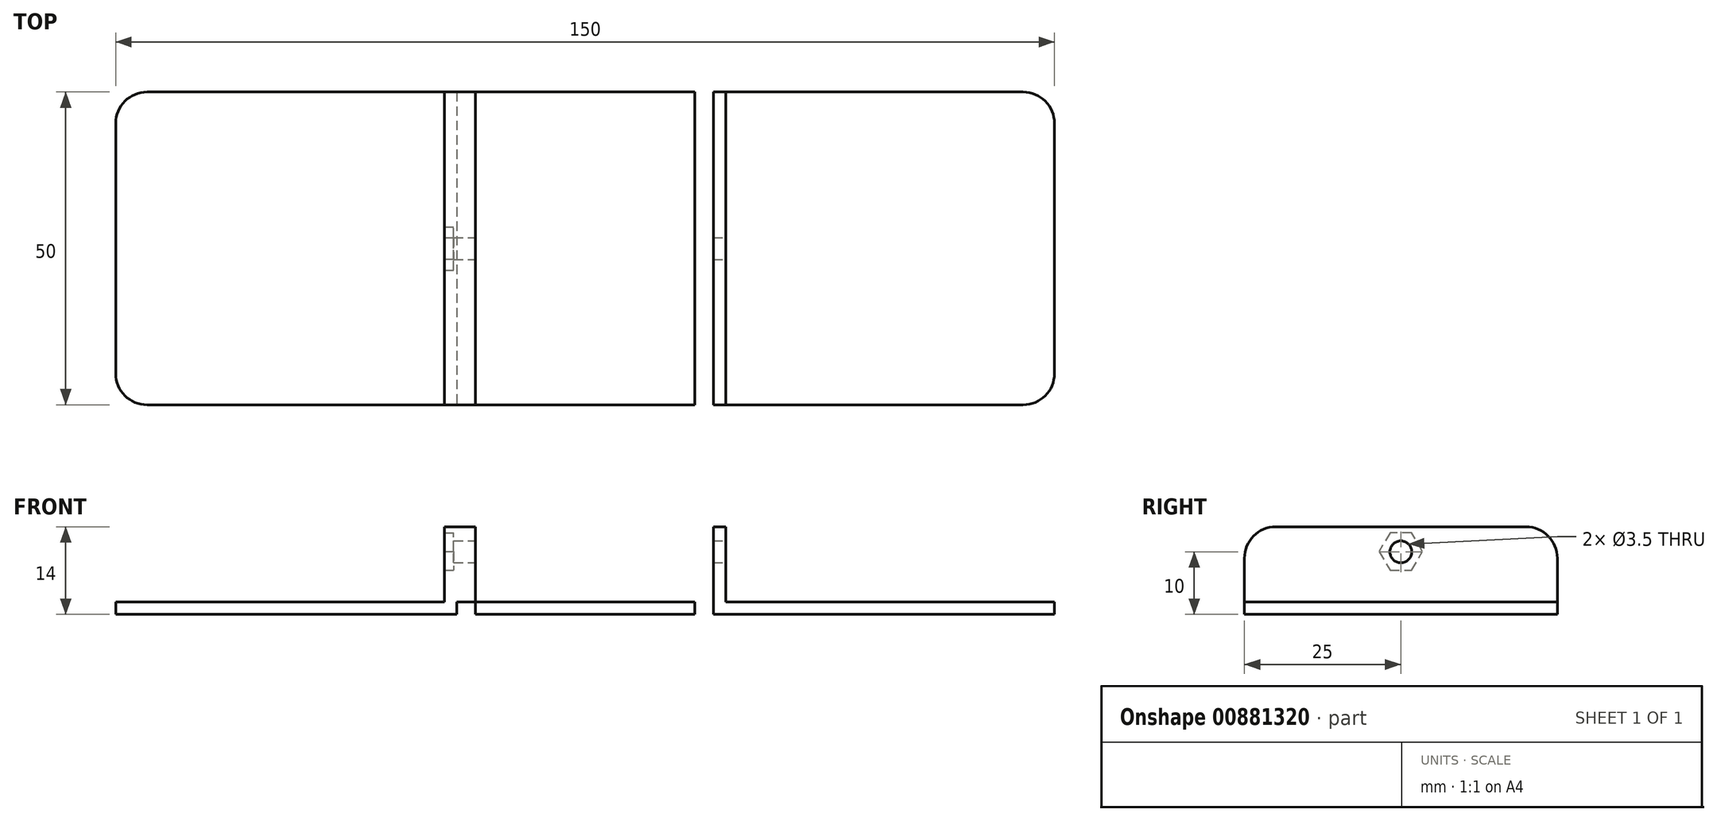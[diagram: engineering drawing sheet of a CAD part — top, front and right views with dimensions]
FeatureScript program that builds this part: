
annotation { "Feature Type Name" : "Feature", "Feature Type Description" : "" }
export const myFeature = defineFeature(function(context is Context, id is Id, definition is map)
    precondition{}
    {
        {
            var Q0;
            Q0=qCreatedBy(makeId("Top.planeOp"),FACE);
            var sketch = newSketch(context, id + "F0", { "sketchPlane" : qUnion([Q0])});
            skLineSegment(sketch, "E0.bottom", {"start": v(75, -25) * mm, "end": v(-75, -25) * mm});
            skLineSegment(sketch, "E0.top", {"start": v(75, 25) * mm, "end": v(-75, 25) * mm});
            skLineSegment(sketch, "E0.left", {"start": v(75, -25) * mm, "end": v(75, 25) * mm});
            skLineSegment(sketch, "E0.right", {"start": v(-75, -25) * mm, "end": v(-75, 25) * mm});
            skPoint(sketch, "E0.middle", {"position": v(0, 0) * mm});
            skPoint(sketch, "E1", {"position": v(0, 25) * mm});
            skPoint(sketch, "E2", {"position": v(0, -25) * mm});
            skPoint(sketch, "E3", {"position": v(17.5, 25) * mm});
            skPoint(sketch, "E4", {"position": v(-17.5, 25) * mm});
            skLineSegment(sketch, "E5.bottom", {"start": v(17.5, 25) * mm, "end": v(20.5, 25) * mm});
            skLineSegment(sketch, "E5.top", {"start": v(17.5, -25) * mm, "end": v(20.5, -25) * mm});
            skLineSegment(sketch, "E5.left", {"start": v(17.5, 25) * mm, "end": v(17.5, -25) * mm});
            skLineSegment(sketch, "E5.right", {"start": v(20.5, 25) * mm, "end": v(20.5, -25) * mm});
            skLineSegment(sketch, "E6.bottom", {"start": v(-17.5, 25) * mm, "end": v(-20.5, 25) * mm});
            skLineSegment(sketch, "E6.top", {"start": v(-17.5, -25) * mm, "end": v(-20.5, -25) * mm});
            skLineSegment(sketch, "E6.left", {"start": v(-17.5, 25) * mm, "end": v(-17.5, -25) * mm});
            skLineSegment(sketch, "E6.right", {"start": v(-20.5, 25) * mm, "end": v(-20.5, -25) * mm});
            skSolve(sketch);
        }
        {
            var Q0;
            {var subQ0=sQuery(id+"F0.wireOp",EDGE,"E0.right");Q0=makeQuery(id+"F0.imprint","IMPRINT",FACE,{"disambiguationData":[TD([[makeQuery(id+"F0.imprint","IMPRINT",EDGE,{"derivedFrom":subQ0}),-1.0]])]});}
            var Q1;
            Q1=makeQuery(id+"F0.imprint","IMPRINT",FACE,{"disambiguationData":[TD([[makeQuery(id+"F0.imprint","IMPRINT",EDGE,{"derivedFrom":sQuery(id+"F0.wireOp",EDGE,"E6.bottom")}),1.0]])]});
            var Q2;
            {var subQ0=sQuery(id+"F0.wireOp",EDGE,"E5.left");Q2=makeQuery(id+"F0.imprint","IMPRINT",FACE,{"disambiguationData":[TD([[makeQuery(id+"F0.imprint","IMPRINT",EDGE,{"derivedFrom":subQ0}),-1.0]])]});}
            var Q3;
            {var subQ0=sQuery(id+"F0.wireOp",EDGE,"E0.left");Q3=makeQuery(id+"F0.imprint","IMPRINT",FACE,{"disambiguationData":[TD([[makeQuery(id+"F0.imprint","IMPRINT",EDGE,{"derivedFrom":subQ0}),1.0]])]});}
            var Q4;
            Q4=makeQuery(id+"F0.imprint","IMPRINT",FACE,{"disambiguationData":[TD([[makeQuery(id+"F0.imprint","IMPRINT",EDGE,{"derivedFrom":sQuery(id+"F0.wireOp",EDGE,"E5.bottom")}),-1.0]])]});
            extrude(context, id + "F1", {"entities" : qUnion([Q0, Q1, Q2, Q3, Q4]), "oppositeDirection" : true, "depth" : 2 * mm});
        }
        {
            var Q0;
            Q0=makeQuery(id+"F1.opExtrude","CAP_FACE",FACE,{"disambiguationData":[OSD([sQuery(id+"F0.wireOp",EDGE,"E0.bottom"),sQuery(id+"F0.wireOp",EDGE,"E0.top"),sQuery(id+"F0.wireOp",EDGE,"E0.left"),sQuery(id+"F0.wireOp",EDGE,"E0.right"),sQuery(id+"F0.wireOp",EDGE,"E5.bottom"),sQuery(id+"F0.wireOp",EDGE,"E5.top"),sQuery(id+"F0.wireOp",EDGE,"E6.bottom"),sQuery(id+"F0.wireOp",EDGE,"E6.top")])],"isStart":true});
            var sketch = newSketch(context, id + "F2", { "sketchPlane" : qUnion([Q0])});
            skPoint(sketch, "E7", {"position": v(0, 25) * mm});
            skPoint(sketch, "E8", {"position": v(17.5, 25) * mm});
            skPoint(sketch, "E9", {"position": v(-17.5, 25) * mm});
            skLineSegment(sketch, "E10.bottom", {"start": v(17.5, 25) * mm, "end": v(21, 25) * mm});
            skLineSegment(sketch, "E10.top", {"start": v(17.5, -25) * mm, "end": v(21, -25) * mm});
            skLineSegment(sketch, "E10.left", {"start": v(17.5, 25) * mm, "end": v(17.5, -25) * mm});
            skLineSegment(sketch, "E10.right", {"start": v(21, 25) * mm, "end": v(21, -25) * mm});
            skLineSegment(sketch, "E11.bottom", {"start": v(-17.5, 25) * mm, "end": v(-21, 25) * mm});
            skLineSegment(sketch, "E11.top", {"start": v(-17.5, -25) * mm, "end": v(-21, -25) * mm});
            skLineSegment(sketch, "E11.left", {"start": v(-17.5, 25) * mm, "end": v(-17.5, -25) * mm});
            skLineSegment(sketch, "E11.right", {"start": v(-21, 25) * mm, "end": v(-21, -25) * mm});
            skSolve(sketch);
        }
        {
            var Q0;
            Q0=makeQuery(id+"F2.imprint","IMPRINT",FACE,{"disambiguationData":[TD([[makeQuery(id+"F2.imprint","IMPRINT",EDGE,{"derivedFrom":sQuery(id+"F2.wireOp",EDGE,"E11.bottom")}),1.0]])]});
            var Q1;
            Q1=makeQuery(id+"F2.imprint","IMPRINT",FACE,{"disambiguationData":[TD([[makeQuery(id+"F2.imprint","IMPRINT",EDGE,{"derivedFrom":sQuery(id+"F2.wireOp",EDGE,"E10.bottom")}),1.0]])]});
            extrude(context, id + "F3", {"entities" : qUnion([Q0, Q1]), "operationType" : NewBodyOperationType.ADD, "depth" : 12 * mm});
        }
        {
            var Q0;
            Q0=makeQuery(id+"F3.opExtrude","SWEPT_FACE",FACE,{"disambiguationData":[OSD([sQuery(id+"F2.wireOp",EDGE,"E11.right")])]});
            var sketch = newSketch(context, id + "F4", { "sketchPlane" : qUnion([Q0])});
            skPoint(sketch, "E12", {"position": v(0, 8) * mm});
            skSolve(sketch);
        }
        {
            var Q0;
            {var subQ0=sQuery(id+"F2.wireOp",EDGE,"E11.right");Q0=makeQuery(id+"F4.imprint","IMPRINT",FACE,{"disambiguationData":[TD([[makeQuery(id+"F4.imprint","IMPRINT",EDGE,{"derivedFrom":makeQuery(id+"F3.opExtrude","CAP_EDGE",EDGE,{"disambiguationData":[OSD([subQ0])],"isStart":false})}),-1.0]])]});}
            var sketch = newSketch(context, id + "F5", { "sketchPlane" : qUnion([Q0])});
            skCircle(sketch, "E13.cCircle", {"center": v(0, 8.07) * mm, "radius": 3 * mm, "construction": true});
            skLineSegment(sketch, "E13.0", {"start": v(1.73, 5.07) * mm, "end": v(-1.73, 5.07) * mm});
            skLineSegment(sketch, "E13.1", {"start": v(-1.73, 5.07) * mm, "end": v(-3.46, 8.07) * mm});
            skLineSegment(sketch, "E13.2", {"start": v(-3.46, 8.07) * mm, "end": v(-1.73, 11.07) * mm});
            skLineSegment(sketch, "E13.3", {"start": v(-1.73, 11.07) * mm, "end": v(1.73, 11.07) * mm});
            skLineSegment(sketch, "E13.4", {"start": v(1.73, 11.07) * mm, "end": v(3.46, 8.07) * mm});
            skLineSegment(sketch, "E13.5", {"start": v(3.46, 8.07) * mm, "end": v(1.73, 5.07) * mm});
            skPoint(sketch, "E13.0.midPoint", {"position": v(0, 5.07) * mm});
            skSolve(sketch);
        }
        {
            var Q0;
            Q0=makeQuery(id+"F5.imprint","IMPRINT",FACE,{"disambiguationData":[TD([[makeQuery(id+"F5.imprint","IMPRINT",EDGE,{"derivedFrom":sQuery(id+"F5.wireOp",EDGE,"E13.0")}),1.0]])]});
            extrude(context, id + "F6", {"entities" : qUnion([Q0]), "operationType" : NewBodyOperationType.ADD, "depth" : 1.5 * mm});
        }
        {
            var Q0;
            Q0=sQuery(id+"F4.wireOp",VERTEX,"E12");
            var Q1;
            Q1=makeQuery(id+"F1.opExtrude","SWEPT_BODY",BODY,{"disambiguationData":[OSD([sQuery(id+"F0.wireOp",EDGE,"E0.bottom"),sQuery(id+"F0.wireOp",EDGE,"E0.top"),sQuery(id+"F0.wireOp",EDGE,"E0.left"),sQuery(id+"F0.wireOp",EDGE,"E0.right"),sQuery(id+"F0.wireOp",EDGE,"E5.bottom"),sQuery(id+"F0.wireOp",EDGE,"E5.top"),sQuery(id+"F0.wireOp",EDGE,"E6.bottom"),sQuery(id+"F0.wireOp",EDGE,"E6.top")])]});
            hole(context, id + "F7", {"style" : HoleStyle.SIMPLE, "endStyle" : HoleEndStyle.THROUGH, "holeDiameter" : 3.5 * mm, "locations" : qUnion([Q0]), "scope" : qUnion([Q1]), "isTappedThrough" : true, "startStyle" : HoleStartStyle.SKETCH});
        }
        {
            var Q0;
            Q0=makeQuery(id+"F1.opExtrude","SWEPT_EDGE",EDGE,{"disambiguationData":[OSD([sQuery(id+"F0.wireOp",EDGE,"E0.bottom"),sQuery(id+"F0.wireOp",EDGE,"E0.right")])]});
            var Q1;
            Q1=makeQuery(id+"F1.opExtrude","SWEPT_EDGE",EDGE,{"disambiguationData":[OSD([sQuery(id+"F0.wireOp",EDGE,"E0.top"),sQuery(id+"F0.wireOp",EDGE,"E0.right")])]});
            var Q2;
            {var subQ0=sQuery(id+"F2.wireOp",EDGE,"E11.right");var subQ1=sQuery(id+"F2.wireOp",EDGE,"E11.bottom");var subQ2=sQuery(id+"F0.wireOp",EDGE,"E6.bottom");var subQ3=sQuery(id+"F0.wireOp",EDGE,"E5.bottom");var subQ4=sQuery(id+"F0.wireOp",EDGE,"E0.top");Q2=makeQuery(id+"F6.boolean.opBoolean","MERGE",EDGE,{"derivedFrom":[makeQuery(id+"F3.opExtrude","CAP_EDGE",EDGE,{"disambiguationData":[OSD([subQ1])],"isStart":false}),makeQuery(id+"F6.opExtrude","SWEPT_EDGE",EDGE,{"disambiguationData":[OSD([subQ4,subQ3,subQ2,subQ1,subQ0]),TDD([makeQuery(id+"F5.imprint","INTERSECT",VERTEX,{"derivedFrom":[makeQuery(id+"F4.imprint","IMPRINT",EDGE,{"derivedFrom":makeQuery(id+"F3.opExtrude","SWEPT_EDGE",EDGE,{"disambiguationData":[OSD([subQ4,subQ3,subQ2,subQ1,subQ0])]})}),makeQuery(id+"F4.imprint","IMPRINT",EDGE,{"derivedFrom":makeQuery(id+"F3.opExtrude","CAP_EDGE",EDGE,{"disambiguationData":[OSD([subQ0])],"isStart":false})})]})])]})]});}
            var Q3;
            Q3=makeQuery(id+"F3.opExtrude","CAP_EDGE",EDGE,{"disambiguationData":[OSD([sQuery(id+"F2.wireOp",EDGE,"E10.bottom")])],"isStart":false});
            var Q4;
            Q4=makeQuery(id+"F1.opExtrude","SWEPT_EDGE",EDGE,{"disambiguationData":[OSD([sQuery(id+"F0.wireOp",EDGE,"E0.top"),sQuery(id+"F0.wireOp",EDGE,"E0.left")])]});
            var Q5;
            Q5=makeQuery(id+"F1.opExtrude","SWEPT_EDGE",EDGE,{"disambiguationData":[OSD([sQuery(id+"F0.wireOp",EDGE,"E0.bottom"),sQuery(id+"F0.wireOp",EDGE,"E0.left")])]});
            var Q6;
            Q6=makeQuery(id+"F3.opExtrude","CAP_EDGE",EDGE,{"disambiguationData":[OSD([sQuery(id+"F2.wireOp",EDGE,"E10.top")])],"isStart":false});
            var Q7;
            {var subQ0=sQuery(id+"F2.wireOp",EDGE,"E11.right");var subQ1=sQuery(id+"F2.wireOp",EDGE,"E11.top");var subQ2=sQuery(id+"F0.wireOp",EDGE,"E6.top");var subQ3=sQuery(id+"F0.wireOp",EDGE,"E5.top");var subQ4=sQuery(id+"F0.wireOp",EDGE,"E0.bottom");Q7=makeQuery(id+"F6.boolean.opBoolean","MERGE",EDGE,{"derivedFrom":[makeQuery(id+"F3.opExtrude","CAP_EDGE",EDGE,{"disambiguationData":[OSD([subQ1])],"isStart":false}),makeQuery(id+"F6.opExtrude","SWEPT_EDGE",EDGE,{"disambiguationData":[OSD([subQ4,subQ3,subQ2,subQ1,subQ0]),TDD([makeQuery(id+"F5.imprint","INTERSECT",VERTEX,{"derivedFrom":[makeQuery(id+"F4.imprint","IMPRINT",EDGE,{"derivedFrom":makeQuery(id+"F3.opExtrude","SWEPT_EDGE",EDGE,{"disambiguationData":[OSD([subQ4,subQ3,subQ2,subQ1,subQ0])]})}),makeQuery(id+"F4.imprint","IMPRINT",EDGE,{"derivedFrom":makeQuery(id+"F3.opExtrude","CAP_EDGE",EDGE,{"disambiguationData":[OSD([subQ0])],"isStart":false})})]})])]})]});}
            fillet(context, id + "F8", {"entities" : qUnion([Q0, Q1, Q2, Q3, Q4, Q5, Q6, Q7]), "radius" : 5 * mm, "tangentPropagation" : true, "allowEdgeOverflow" : false});
        }
        {
            var Q0;
            Q0=makeQuery(id+"F3.opExtrude","SWEPT_FACE",FACE,{"disambiguationData":[OSD([sQuery(id+"F2.wireOp",EDGE,"E10.right")])]});
            extrude(context, id + "F9", {"entities" : qUnion([Q0]), "operationType" : NewBodyOperationType.ADD, "depth" : 1.5 * mm});
        }
    });
